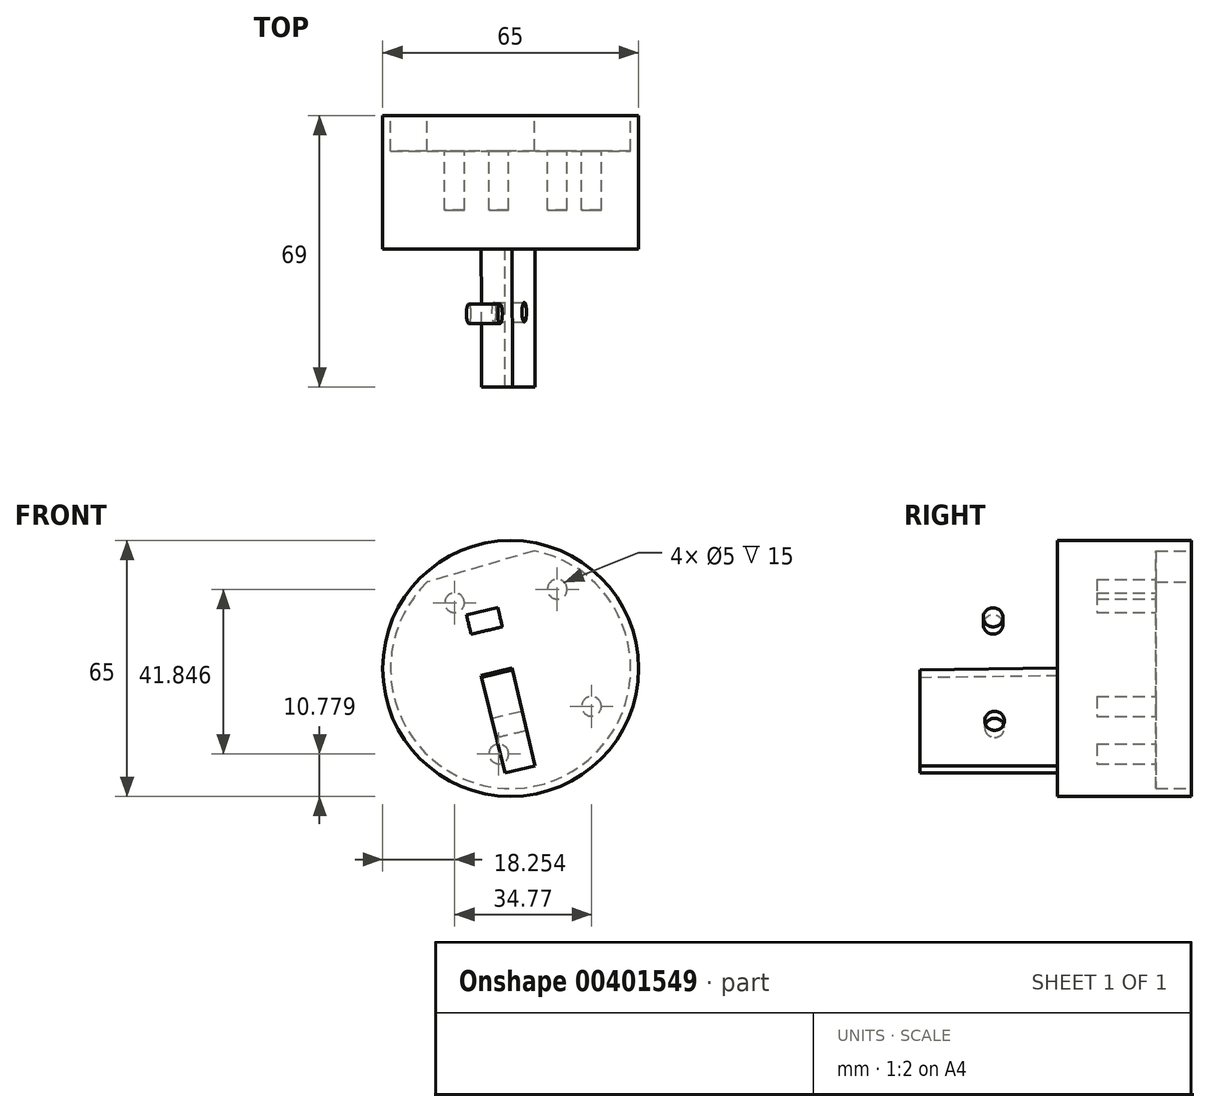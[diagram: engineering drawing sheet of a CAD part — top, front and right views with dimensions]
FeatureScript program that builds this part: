
annotation { "Feature Type Name" : "Feature", "Feature Type Description" : "" }
export const myFeature = defineFeature(function(context is Context, id is Id, definition is map)
    precondition{}
    {
        {
            var Q0;
            Q0=qCreatedBy(makeId("Front.planeOp"),FACE);
            var sketch = newSketch(context, id + "F0", { "sketchPlane" : qUnion([Q0])});
            skArc(sketch, "E0", {"start": v(-21.19, 21.94) * mm, "mid": v(8.55, -29.28) * mm, "end": v(6.05, 29.9) * mm});
            skLineSegment(sketch, "E1", {"start": v(6.05, 29.9) * mm, "end": v(-21.19, 21.94) * mm});
            skCircle(sketch, "E2", {"center": v(0, 0) * mm, "radius": 32.5 * mm});
            skSolve(sketch);
        }
        {
            var Q0;
            Q0=makeQuery(id+"F0.imprint","IMPRINT",FACE,{"disambiguationData":[TD([[makeQuery(id+"F0.imprint","IMPRINT",EDGE,{"derivedFrom":sQuery(id+"F0.wireOp",EDGE,"E0")}),-1.0]])]});
            extrude(context, id + "F1", {"entities" : qUnion([Q0]), "depth" : 9 * mm});
        }
        {
            var Q0;
            Q0=makeQuery(id+"F1.opExtrude","CAP_FACE",FACE,{"disambiguationData":[OSD([sQuery(id+"F0.wireOp",EDGE,"E0"),sQuery(id+"F0.wireOp",EDGE,"E1"),sQuery(id+"F0.wireOp",EDGE,"E2")])],"isStart":false});
            var sketch = newSketch(context, id + "F2", { "sketchPlane" : qUnion([Q0])});
            skCircle(sketch, "E3", {"center": v(0, 0) * mm, "radius": 32.5 * mm});
            skSolve(sketch);
        }
        {
            var Q0;
            Q0 = qSketchRegion(id + "F2", true);
            extrude(context, id + "F3", {"entities" : qUnion([Q0]), "operationType" : NewBodyOperationType.ADD, "depth" : 25 * mm});
        }
        {
            var Q0;
            Q0=makeQuery(id+"F3.opExtrude","CAP_FACE",FACE,{"disambiguationData":[OSD([sQuery(id+"F2.wireOp",EDGE,"E3")])],"isStart":false});
            var sketch = newSketch(context, id + "F4", { "sketchPlane" : qUnion([Q0])});
            skSolve(sketch);
        }
        {
            var Q0;
            Q0=makeQuery(id+"F4.imprint","IMPRINT",FACE,{"disambiguationData":[TD([[makeQuery(id+"F4.imprint","IMPRINT",EDGE,{"derivedFrom":makeQuery(id+"F3.opExtrude","CAP_EDGE",EDGE,{"disambiguationData":[OSD([sQuery(id+"F2.wireOp",EDGE,"E3")])],"isStart":false})}),1.0]])]});
            var sketch = newSketch(context, id + "F5", { "sketchPlane" : qUnion([Q0])});
            skArc(sketch, "E4", {"start": v(-7.07, 31.72) * mm, "mid": v(-31.65, -7.4) * mm, "end": v(7.71, -31.57) * mm});
            skLineSegment(sketch, "E5", {"start": v(-7.07, 31.72) * mm, "end": v(7.71, -31.57) * mm});
            skSolve(sketch);
        }
        {
            var Q0;
            Q0 = qSketchRegion(id + "F5", true);
            extrude(context, id + "F6", {"entities" : qUnion([Q0]), "operationType" : NewBodyOperationType.ADD, "depth" : 35 * mm});
        }
        {
            var Q0;
            Q0=makeQuery(id+"F6.opExtrude","CAP_FACE",FACE,{"disambiguationData":[OSD([sQuery(id+"F5.wireOp",EDGE,"E4"),sQuery(id+"F5.wireOp",EDGE,"E5")])],"isStart":false});
            var sketch = newSketch(context, id + "F7", { "sketchPlane" : qUnion([Q0])});
            skArc(sketch, "E6.0.1", {"start": v(-14.97, 28.85) * mm, "mid": v(-31.57, -7.7) * mm, "end": v(0, -32.5) * mm});
            skLineSegment(sketch, "E7", {"start": v(0, -32.5) * mm, "end": v(-14.97, 28.85) * mm});
            skPoint(sketch, "E6.0.0.start.orphan", {"position": v(7.71, -31.57) * mm});
            skPoint(sketch, "E8.orphan", {"position": v(-7.07, 31.72) * mm});
            skSolve(sketch);
        }
        {
            var Q0;
            Q0=makeQuery(id+"F7.imprint","IMPRINT",FACE,{"disambiguationData":[TD([[makeQuery(id+"F7.imprint","IMPRINT",EDGE,{"derivedFrom":sQuery(id+"F7.wireOp",EDGE,"E6.0.1")}),1.0]])]});
            extrude(context, id + "F8", {"entities" : qUnion([Q0]), "operationType" : NewBodyOperationType.REMOVE, "oppositeDirection" : true, "depth" : 35 * mm});
        }
        {
            var Q0;
            Q0=makeQuery(id+"F6.opExtrude","SWEPT_FACE",FACE,{"disambiguationData":[OSD([sQuery(id+"F5.wireOp",EDGE,"E5")])]});
            var sketch = newSketch(context, id + "F9", { "sketchPlane" : qUnion([Q0])});
            skLineSegment(sketch, "E9.left", {"start": v(-34, -32.5) * mm, "end": v(-34, -25.5) * mm});
            skLineSegment(sketch, "E9.right", {"start": v(-69, -32.5) * mm, "end": v(-69, -25.5) * mm});
            skLineSegment(sketch, "E10", {"start": v(-69, -25.5) * mm, "end": v(-34, -25.5) * mm});
            skLineSegment(sketch, "E11", {"start": v(-69, 24.5) * mm, "end": v(-34, 24.5) * mm});
            skLineSegment(sketch, "E12.trimOffspring", {"start": v(-69, 24.5) * mm, "end": v(-69, 32.5) * mm});
            skLineSegment(sketch, "E13.trimOffspring", {"start": v(-34, 24.5) * mm, "end": v(-34, 32.5) * mm});
            skLineSegment(sketch, "E14.top", {"start": v(-69, -40.38) * mm, "end": v(-34, -40.38) * mm});
            skLineSegment(sketch, "E14.left", {"start": v(-69, -25.5) * mm, "end": v(-69, -40.38) * mm});
            skLineSegment(sketch, "E14.right", {"start": v(-34, -25.5) * mm, "end": v(-34, -40.38) * mm});
            skLineSegment(sketch, "E15.top", {"start": v(-69, 45.28) * mm, "end": v(-34, 45.28) * mm});
            skLineSegment(sketch, "E15.left", {"start": v(-69, 32.5) * mm, "end": v(-69, 45.28) * mm});
            skLineSegment(sketch, "E15.right", {"start": v(-34, 32.5) * mm, "end": v(-34, 45.28) * mm});
            skSolve(sketch);
        }
        {
            var Q0;
            Q0 = qSketchRegion(id + "F9", true);
            extrude(context, id + "F10", {"entities" : qUnion([Q0]), "operationType" : NewBodyOperationType.REMOVE, "oppositeDirection" : true, "depth" : 25 * mm});
        }
        {
            var Q0;
            Q0=makeQuery(id+"F6.opExtrude","SWEPT_FACE",FACE,{"disambiguationData":[OSD([sQuery(id+"F5.wireOp",EDGE,"E5")])]});
            var sketch = newSketch(context, id + "F11", { "sketchPlane" : qUnion([Q0])});
            skCircle(sketch, "E16", {"center": v(-50, -13.73) * mm, "radius": 2.5 * mm});
            skLineSegment(sketch, "E17", {"start": v(-69, -0.5) * mm, "end": v(-34, 0) * mm});
            skPoint(sketch, "E17.endSnap0", {"position": v(-34, -0.5) * mm});
            skCircle(sketch, "E18.MirrorC", {"center": v(-50.38, 13.27) * mm, "radius": 2.5 * mm});
            skSolve(sketch);
        }
        {
            var Q0;
            Q0=makeQuery(id+"F11.imprint","IMPRINT",FACE,{"disambiguationData":[TD([[makeQuery(id+"F11.imprint","IMPRINT",EDGE,{"derivedFrom":sQuery(id+"F11.wireOp",EDGE,"E16")}),1.0]])]});
            var Q1;
            Q1=makeQuery(id+"F11.imprint","IMPRINT",FACE,{"disambiguationData":[TD([[makeQuery(id+"F11.imprint","IMPRINT",EDGE,{"derivedFrom":sQuery(id+"F11.wireOp",EDGE,"E18.MirrorC")}),-1.0]])]});
            extrude(context, id + "F12", {"entities" : qUnion([Q0, Q1]), "operationType" : NewBodyOperationType.REMOVE, "oppositeDirection" : true, "depth" : 25 * mm});
        }
        {
            var Q0;
            Q0=makeQuery(id+"F3.opExtrude","CAP_FACE",FACE,{"disambiguationData":[OSD([sQuery(id+"F2.wireOp",EDGE,"E3")])],"isStart":true});
            var sketch = newSketch(context, id + "F13", { "sketchPlane" : qUnion([Q0])});
            skCircle(sketch, "E19", {"center": v(-11.83, 20.12) * mm, "radius": 2.5 * mm});
            skLineSegment(sketch, "E20", {"start": v(7.57, 25.92) * mm, "end": v(-8.55, -29.28) * mm});
            skCircle(sketch, "E21", {"center": v(-20.52, -9.63) * mm, "radius": 2.5 * mm});
            skLineSegment(sketch, "E22", {"start": v(0, 0) * mm, "end": v(21.2, -6.2) * mm});
            skCircle(sketch, "E23", {"center": v(3.03, -21.72) * mm, "radius": 2.5 * mm});
            skCircle(sketch, "E24", {"center": v(14.25, 16.67) * mm, "radius": 2.5 * mm});
            skSolve(sketch);
        }
        {
            var Q0;
            Q0=makeQuery(id+"F13.imprint","IMPRINT",FACE,{"disambiguationData":[TD([[makeQuery(id+"F13.imprint","IMPRINT",EDGE,{"derivedFrom":sQuery(id+"F13.wireOp",EDGE,"E21")}),1.0]])]});
            var Q1;
            Q1=makeQuery(id+"F13.imprint","IMPRINT",FACE,{"disambiguationData":[TD([[makeQuery(id+"F13.imprint","IMPRINT",EDGE,{"derivedFrom":sQuery(id+"F13.wireOp",EDGE,"E19")}),1.0]])]});
            var Q2;
            Q2=makeQuery(id+"F13.imprint","IMPRINT",FACE,{"disambiguationData":[TD([[makeQuery(id+"F13.imprint","IMPRINT",EDGE,{"derivedFrom":sQuery(id+"F13.wireOp",EDGE,"E24")}),1.0]])]});
            var Q3;
            Q3=makeQuery(id+"F13.imprint","IMPRINT",FACE,{"disambiguationData":[TD([[makeQuery(id+"F13.imprint","IMPRINT",EDGE,{"derivedFrom":sQuery(id+"F13.wireOp",EDGE,"E23")}),1.0]])]});
            extrude(context, id + "F14", {"entities" : qUnion([Q0, Q1, Q2, Q3]), "operationType" : NewBodyOperationType.REMOVE, "oppositeDirection" : true, "depth" : 15 * mm});
        }
    });
